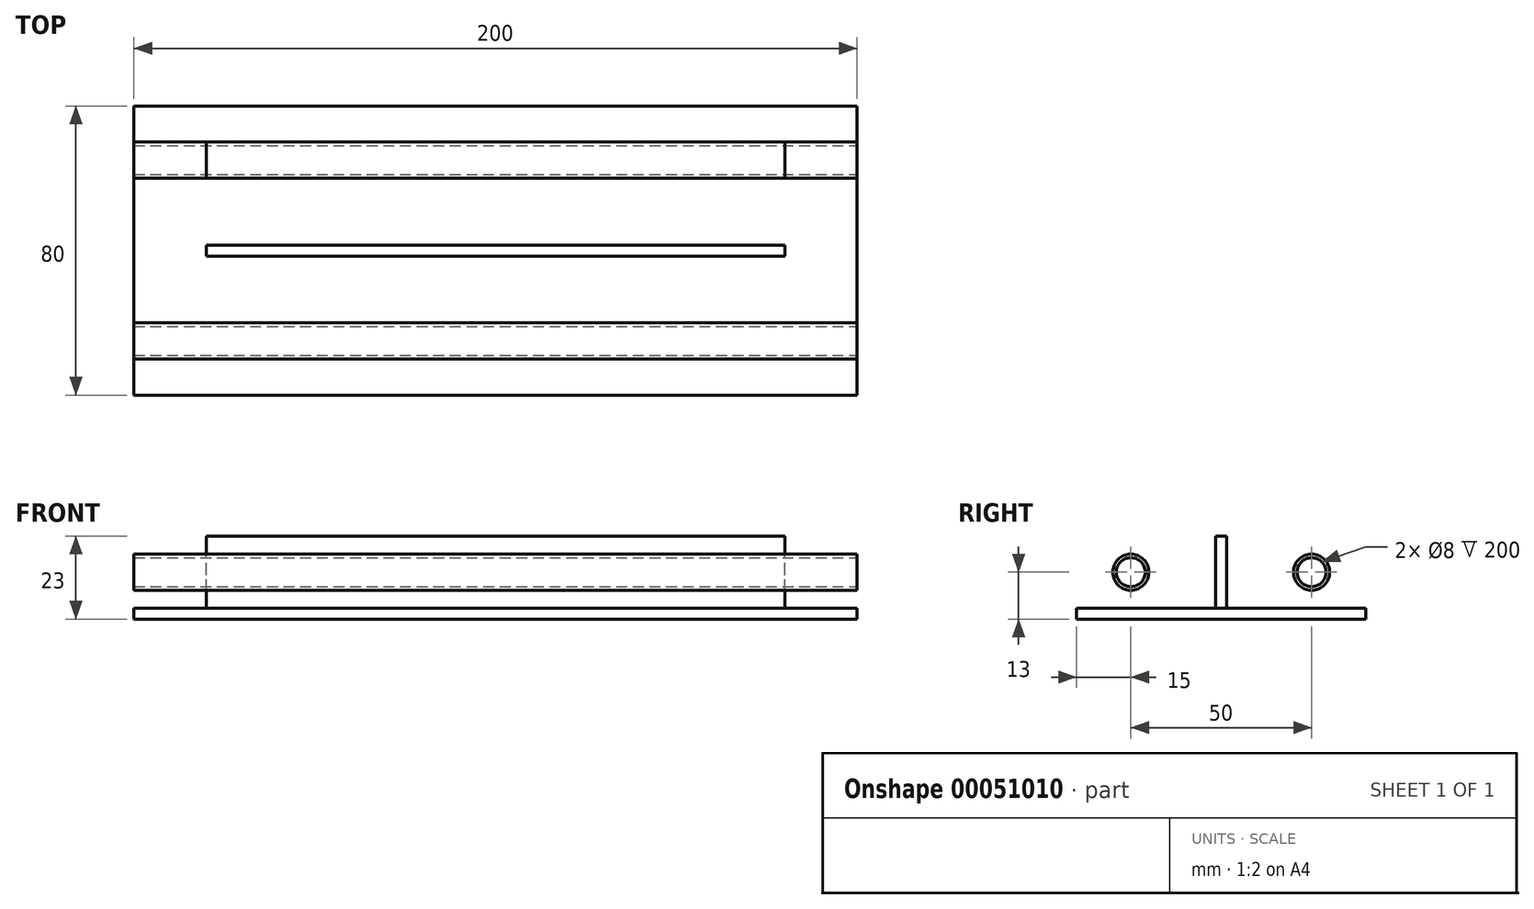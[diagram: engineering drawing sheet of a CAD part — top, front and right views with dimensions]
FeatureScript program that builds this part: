
annotation { "Feature Type Name" : "Feature", "Feature Type Description" : "" }
export const myFeature = defineFeature(function(context is Context, id is Id, definition is map)
    precondition{}
    {
        {
            var Q0;
            Q0=qCreatedBy(makeId("Top.planeOp"),FACE);
            var sketch = newSketch(context, id + "F0", { "sketchPlane" : qUnion([Q0])});
            skLineSegment(sketch, "E0.rect.bottom", {"start": v(-100, -40) * mm, "end": v(100, -40) * mm});
            skLineSegment(sketch, "E0.rect.top", {"start": v(-100, 40) * mm, "end": v(100, 40) * mm});
            skLineSegment(sketch, "E0.rect.left", {"start": v(-100, -40) * mm, "end": v(-100, 40) * mm});
            skLineSegment(sketch, "E0.rect.right", {"start": v(100, -40) * mm, "end": v(100, 40) * mm});
            skPoint(sketch, "E0.rect.middle", {"position": v(0, 0) * mm});
            skSolve(sketch);
        }
        {
            var Q0;
            Q0=makeQuery(id+"F0.imprint","IMPRINT",FACE,{"disambiguationData":[TD([[makeQuery(id+"F0.imprint","IMPRINT",EDGE,{"derivedFrom":sQuery(id+"F0.wireOp",EDGE,"E0.rect.bottom")}),1.0]])]});
            extrude(context, id + "F1", {"entities" : qUnion([Q0]), "oppositeDirection" : true, "depth" : 3 * mm});
        }
        {
            var Q0;
            Q0=makeQuery(id+"F1.opExtrude","CAP_FACE",FACE,{"disambiguationData":[OSD([sQuery(id+"F0.wireOp",EDGE,"E0.rect.bottom"),sQuery(id+"F0.wireOp",EDGE,"E0.rect.top"),sQuery(id+"F0.wireOp",EDGE,"E0.rect.left"),sQuery(id+"F0.wireOp",EDGE,"E0.rect.right")])],"isStart":true});
            var sketch = newSketch(context, id + "F2", { "sketchPlane" : qUnion([Q0])});
            skLineSegment(sketch, "E1.bottom", {"start": v(100, 40) * mm, "end": v(80, 40) * mm});
            skLineSegment(sketch, "E1.top", {"start": v(100, -40) * mm, "end": v(80, -40) * mm});
            skLineSegment(sketch, "E1.left", {"start": v(100, 40) * mm, "end": v(100, -40) * mm});
            skLineSegment(sketch, "E1.right", {"start": v(80, 40) * mm, "end": v(80, -40) * mm});
            skSolve(sketch);
        }
        {
            var Q0;
            Q0=makeQuery(id+"F2.imprint","IMPRINT",FACE,{"disambiguationData":[TD([[makeQuery(id+"F2.imprint","IMPRINT",EDGE,{"derivedFrom":sQuery(id+"F2.wireOp",EDGE,"E1.bottom")}),-1.0]])]});
            extrude(context, id + "F3", {"entities" : qUnion([Q0]), "depth" : 20 * mm});
        }
        {
            var Q0;
            Q0=makeQuery(id+"F3.opExtrude","SWEPT_FACE",FACE,{"disambiguationData":[OSD([sQuery(id+"F2.wireOp",EDGE,"E1.left")])]});
            var sketch = newSketch(context, id + "F4", { "sketchPlane" : qUnion([Q0])});
            skCircle(sketch, "E2", {"center": v(-25, 10) * mm, "radius": 5 * mm});
            skLineSegment(sketch, "E3", {"start": v(0, 0) * mm, "end": v(0, 20) * mm, "construction": true});
            skCircle(sketch, "E4.MirrorC", {"center": v(25, 10) * mm, "radius": 5 * mm});
            skSolve(sketch);
        }
        {
            var Q0;
            Q0=makeQuery(id+"F4.imprint","IMPRINT",FACE,{"disambiguationData":[TD([[makeQuery(id+"F4.imprint","IMPRINT",EDGE,{"derivedFrom":sQuery(id+"F4.wireOp",EDGE,"E2")}),1.0]])]});
            var Q1;
            Q1=makeQuery(id+"F4.imprint","IMPRINT",FACE,{"disambiguationData":[TD([[makeQuery(id+"F4.imprint","IMPRINT",EDGE,{"derivedFrom":sQuery(id+"F4.wireOp",EDGE,"E4.MirrorC")}),-1.0]])]});
            var Q2;
            Q2=sQuery(id+"F4.wireOp",EDGE,"E2");
            extrude(context, id + "F5", {"entities" : qUnion([Q0, Q1]), "operationType" : NewBodyOperationType.REMOVE, "surfaceEntities" : qUnion([Q2]), "oppositeDirection" : true, "depth" : 25 * mm});
        }
        {
            var Q0;
            Q0=makeQuery(id+"F3.opExtrude","SWEPT_BODY",BODY,{"disambiguationData":[OSD([sQuery(id+"F2.wireOp",EDGE,"E1.bottom"),sQuery(id+"F2.wireOp",EDGE,"E1.top"),sQuery(id+"F2.wireOp",EDGE,"E1.left"),sQuery(id+"F2.wireOp",EDGE,"E1.right")])]});
            var Q1;
            Q1=qCreatedBy(makeId("Right.planeOp"),FACE);
            mirror(context, id + "F6", {"entities" : qUnion([Q0]), "mirrorPlane" : qUnion([Q1])});
        }
        {
            var Q0;
            Q0=qCreatedBy(makeId("Front.planeOp"),FACE);
            var sketch = newSketch(context, id + "F7", { "sketchPlane" : qUnion([Q0])});
            skLineSegment(sketch, "E5.bottom", {"start": v(-80, 0) * mm, "end": v(80, 0) * mm});
            skLineSegment(sketch, "E5.top", {"start": v(-80, 20) * mm, "end": v(80, 20) * mm});
            skLineSegment(sketch, "E5.left", {"start": v(-80, 0) * mm, "end": v(-80, 20) * mm});
            skLineSegment(sketch, "E5.right", {"start": v(80, 0) * mm, "end": v(80, 20) * mm});
            skPoint(sketch, "E6.0", {"position": v(80, 20) * mm});
            skPoint(sketch, "E6.1", {"position": v(80, 0) * mm});
            skSolve(sketch);
        }
        {
            var Q0;
            Q0=makeQuery(id+"F7.imprint","IMPRINT",FACE,{"disambiguationData":[TD([[makeQuery(id+"F7.imprint","IMPRINT",EDGE,{"derivedFrom":sQuery(id+"F7.wireOp",EDGE,"E5.bottom")}),1.0]])]});
            var Q1;
            Q1=sQuery(id+"F7.wireOp",EDGE,"E5.top");
            extrude(context, id + "F8", {"entities" : qUnion([Q0]), "surfaceEntities" : qUnion([Q1]), "depth" : 3 * mm, "symmetric" : true});
        }
        {
            var Q0;
            Q0=makeQuery(id+"F4.imprint","IMPRINT",FACE,{"disambiguationData":[TD([[makeQuery(id+"F4.imprint","IMPRINT",EDGE,{"derivedFrom":sQuery(id+"F4.wireOp",EDGE,"E2")}),-1.0]])]});
            var sketch = newSketch(context, id + "F9", { "sketchPlane" : qUnion([Q0])});
            skCircle(sketch, "E7", {"center": v(-25, 10) * mm, "radius": 5 * mm});
            skCircle(sketch, "E8", {"center": v(-25, 10) * mm, "radius": 4 * mm});
            skSolve(sketch);
        }
        {
            var Q0;
            Q0=makeQuery(id+"F9.imprint","IMPRINT",FACE,{"disambiguationData":[TD([[makeQuery(id+"F9.imprint","IMPRINT",EDGE,{"derivedFrom":sQuery(id+"F9.wireOp",EDGE,"E7")}),1.0]])]});
            var Q1;
            Q1=makeQuery(id+"F6.opPattern","COPY",FACE,{"derivedFrom":makeQuery(id+"F3.opExtrude","SWEPT_FACE",FACE,{"disambiguationData":[OSD([sQuery(id+"F2.wireOp",EDGE,"E1.left")])]}),"instanceName":"1"});
            extrude(context, id + "F10", {"entities" : qUnion([Q0]), "endBound" : BoundingType.UP_TO_SURFACE, "oppositeDirection" : true, "endBoundEntityFace" : qUnion([Q1]), "depth" : 250 * mm});
        }
        {
            var Q0;
            Q0=makeQuery(id+"F10.opExtrude","SWEPT_BODY",BODY,{"disambiguationData":[OSD([sQuery(id+"F9.wireOp",EDGE,"E7"),sQuery(id+"F9.wireOp",EDGE,"E8")])]});
            var Q1;
            Q1=qCreatedBy(makeId("Front.planeOp"),FACE);
            mirror(context, id + "F11", {"entities" : qUnion([Q0]), "mirrorPlane" : qUnion([Q1])});
        }
    });
